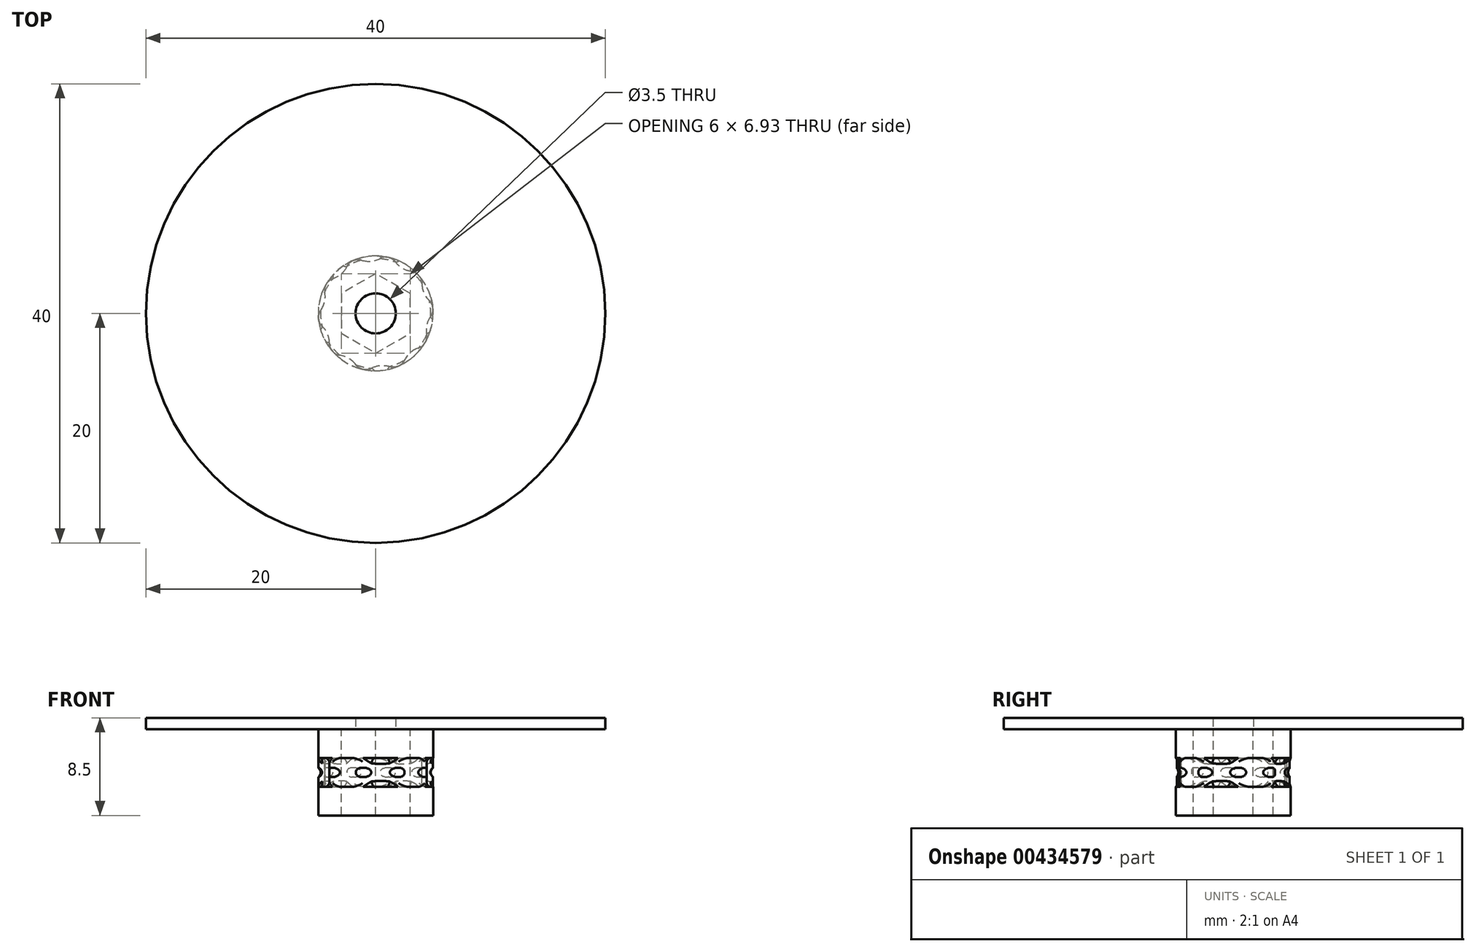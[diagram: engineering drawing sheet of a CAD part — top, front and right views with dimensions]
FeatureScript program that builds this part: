
annotation { "Feature Type Name" : "Feature", "Feature Type Description" : "" }
export const myFeature = defineFeature(function(context is Context, id is Id, definition is map)
    precondition{}
    {
        {
            var Q0;
            Q0=qCreatedBy(makeId("Top.planeOp"),FACE);
            var sketch = newSketch(context, id + "F0", { "sketchPlane" : qUnion([Q0])});
            skCircle(sketch, "E0", {"center": v(0, 0) * mm, "radius": 20 * mm});
            skCircle(sketch, "E1", {"center": v(0, 0) * mm, "radius": 1.75 * mm});
            skSolve(sketch);
        }
        {
            var Q0;
            Q0=makeQuery(id+"F0.imprint","IMPRINT",FACE,{"disambiguationData":[TD([[makeQuery(id+"F0.imprint","IMPRINT",EDGE,{"derivedFrom":sQuery(id+"F0.wireOp",EDGE,"E0")}),1.0]])]});
            extrude(context, id + "F1", {"entities" : qUnion([Q0]), "depth" : 1 * mm});
        }
        {
            var Q0;
            Q0=makeQuery(id+"F1.opExtrude","CAP_FACE",FACE,{"disambiguationData":[OSD([sQuery(id+"F0.wireOp",EDGE,"E0"),sQuery(id+"F0.wireOp",EDGE,"E1")])],"isStart":true});
            var sketch = newSketch(context, id + "F2", { "sketchPlane" : qUnion([Q0])});
            skCircle(sketch, "E2", {"center": v(0, 0) * mm, "radius": 5 * mm});
            skSolve(sketch);
        }
        {
            var Q0;
            Q0=makeQuery(id+"F2.imprint","IMPRINT",FACE,{"disambiguationData":[TD([[makeQuery(id+"F2.imprint","IMPRINT",EDGE,{"derivedFrom":sQuery(id+"F2.wireOp",EDGE,"E2")}),1.0]])]});
            var Q1;
            Q1=makeQuery(id+"F2.imprint","IMPRINT",FACE,{"disambiguationData":[TD([[makeQuery(id+"F2.imprint","IMPRINT",EDGE,{"derivedFrom":makeQuery(id+"F1.opExtrude","CAP_EDGE",EDGE,{"disambiguationData":[OSD([sQuery(id+"F0.wireOp",EDGE,"E1")])],"isStart":true})}),-1.0]])]});
            extrude(context, id + "F3", {"entities" : qUnion([Q0, Q1]), "depth" : 7.5 * mm, "offsetDistance" : 25 * mm});
        }
        {
            var Q0;
            Q0=makeQuery(id+"F3.opExtrude","CAP_FACE",FACE,{"disambiguationData":[OSD([sQuery(id+"F2.wireOp",EDGE,"E2")])],"isStart":true});
            var sketch = newSketch(context, id + "F4", { "sketchPlane" : qUnion([Q0])});
            skCircle(sketch, "E3.cCircle", {"center": v(0, 0) * mm, "radius": 3 * mm, "construction": true});
            skLineSegment(sketch, "E3.0", {"start": v(-3, -1.73) * mm, "end": v(-3, 1.73) * mm});
            skLineSegment(sketch, "E3.1", {"start": v(-3, 1.73) * mm, "end": v(0, 3.46) * mm});
            skLineSegment(sketch, "E3.2", {"start": v(0, 3.46) * mm, "end": v(3, 1.73) * mm});
            skLineSegment(sketch, "E3.3", {"start": v(3, 1.73) * mm, "end": v(3, -1.73) * mm});
            skLineSegment(sketch, "E3.4", {"start": v(3, -1.73) * mm, "end": v(0, -3.46) * mm});
            skLineSegment(sketch, "E3.5", {"start": v(0, -3.46) * mm, "end": v(-3, -1.73) * mm});
            skPoint(sketch, "E3.0.midPoint", {"position": v(-3, 0) * mm});
            skSolve(sketch);
        }
        {
            var Q0;
            Q0 = qSketchRegion(id + "F4", true);
            extrude(context, id + "F5", {"entities" : qUnion([Q0]), "operationType" : NewBodyOperationType.REMOVE, "endBound" : BoundingType.THROUGH_ALL, "oppositeDirection" : true, "depth" : 25 * mm});
        }
        {
            var Q0;
            Q0=makeQuery(id+"F3.opExtrude","CAP_FACE",FACE,{"disambiguationData":[OSD([sQuery(id+"F2.wireOp",EDGE,"E2")])],"isStart":false});
            cPlane(context, id + "F6", {"entities" : qUnion([Q0]), "cplaneType" : CPlaneType.OFFSET, "offset" : 3.75 * mm, "oppositeDirection" : true, "width" : 150 * mm, "height" : 150 * mm});
        }
        {
            var Q0;
            Q0=qCreatedBy(id+"F6.planeOp",FACE);
            var sketch = newSketch(context, id + "F7", { "sketchPlane" : qUnion([Q0])});
            skArc(sketch, "E4", {"start": v(-4.66, 1.12) * mm, "mid": v(-4.98, 0.5) * mm, "end": v(-4.8, -0.19) * mm});
            skArc(sketch, "E5", {"start": v(-4.66, 1.12) * mm, "mid": v(-4.2, 1.8) * mm, "end": v(-4.03, 2.6) * mm});
            skArc(sketch, "E6", {"start": v(-3.17, 3.6) * mm, "mid": v(-3.79, 3.27) * mm, "end": v(-4.03, 2.6) * mm});
            skPoint(sketch, "E7", {"position": v(-3.79, 3.27) * mm});
            skPoint(sketch, "E8", {"position": v(-4.2, 1.8) * mm});
            skPoint(sketch, "E9.positionSnap0", {"position": v(-4.98, 0.5) * mm});
            skCircle(sketch, "E10", {"center": v(0, 0) * mm, "radius": 5 * mm});
            skSolve(sketch);
        }
        {
            var Q0;
            {var subQ0=sQuery(id+"F7.wireOp",EDGE,"E5");Q0=makeQuery(id+"F7.imprint","IMPRINT",FACE,{"disambiguationData":[TD([[makeQuery(id+"F7.imprint","IMPRINT",EDGE,{"derivedFrom":subQ0}),1.0]])]});}
            extrude(context, id + "F8", {"entities" : qUnion([Q0]), "endBound" : BoundingType.SYMMETRIC, "depth" : 2.5 * mm});
        }
        {
            var Q0;
            Q0=qCreatedBy(makeId("Right.planeOp"),FACE);
            var sketch = newSketch(context, id + "F9", { "sketchPlane" : qUnion([Q0])});
            skLineSegment(sketch, "E11", {"start": v(0, 0) * mm, "end": v(0, -12.8) * mm});
            skSolve(sketch);
        }
        {
            var Q0;
            Q0=makeQuery(id+"F8.opExtrude","SWEPT_BODY",BODY,{"disambiguationData":[OSD([sQuery(id+"F7.wireOp",EDGE,"E4"),sQuery(id+"F7.wireOp",EDGE,"E5"),sQuery(id+"F7.wireOp",EDGE,"E6"),sQuery(id+"F7.wireOp",EDGE,"E10")])]});
            var Q1;
            Q1=sQuery(id+"F9.wireOp",EDGE,"E11");
            circularPattern(context, id + "F10", {"entities" : qUnion([Q0]), "axis" : qUnion([Q1]), "angle" : 360 * degree, "instanceCount" : 10, "equalSpace" : true});
        }
        {
            var Q0;
            Q0=makeQuery(id+"F10.opPattern","COPY",BODY,{"derivedFrom":makeQuery(id+"F8.opExtrude","SWEPT_BODY",BODY,{"disambiguationData":[OSD([sQuery(id+"F7.wireOp",EDGE,"E4"),sQuery(id+"F7.wireOp",EDGE,"E5"),sQuery(id+"F7.wireOp",EDGE,"E6"),sQuery(id+"F7.wireOp",EDGE,"E10")])]}),"instanceName":"6"});
            var Q1;
            Q1=makeQuery(id+"F10.opPattern","COPY",BODY,{"derivedFrom":makeQuery(id+"F8.opExtrude","SWEPT_BODY",BODY,{"disambiguationData":[OSD([sQuery(id+"F7.wireOp",EDGE,"E4"),sQuery(id+"F7.wireOp",EDGE,"E5"),sQuery(id+"F7.wireOp",EDGE,"E6"),sQuery(id+"F7.wireOp",EDGE,"E10")])]}),"instanceName":"5"});
            var Q2;
            Q2=makeQuery(id+"F10.opPattern","COPY",BODY,{"derivedFrom":makeQuery(id+"F8.opExtrude","SWEPT_BODY",BODY,{"disambiguationData":[OSD([sQuery(id+"F7.wireOp",EDGE,"E4"),sQuery(id+"F7.wireOp",EDGE,"E5"),sQuery(id+"F7.wireOp",EDGE,"E6"),sQuery(id+"F7.wireOp",EDGE,"E10")])]}),"instanceName":"7"});
            var Q3;
            Q3=makeQuery(id+"F10.opPattern","COPY",BODY,{"derivedFrom":makeQuery(id+"F8.opExtrude","SWEPT_BODY",BODY,{"disambiguationData":[OSD([sQuery(id+"F7.wireOp",EDGE,"E4"),sQuery(id+"F7.wireOp",EDGE,"E5"),sQuery(id+"F7.wireOp",EDGE,"E6"),sQuery(id+"F7.wireOp",EDGE,"E10")])]}),"instanceName":"24"});
            var Q4;
            Q4=makeQuery(id+"F10.opPattern","COPY",BODY,{"derivedFrom":makeQuery(id+"F8.opExtrude","SWEPT_BODY",BODY,{"disambiguationData":[OSD([sQuery(id+"F7.wireOp",EDGE,"E4"),sQuery(id+"F7.wireOp",EDGE,"E5"),sQuery(id+"F7.wireOp",EDGE,"E6"),sQuery(id+"F7.wireOp",EDGE,"E10")])]}),"instanceName":"23"});
            var Q5;
            Q5=makeQuery(id+"F10.opPattern","COPY",BODY,{"derivedFrom":makeQuery(id+"F8.opExtrude","SWEPT_BODY",BODY,{"disambiguationData":[OSD([sQuery(id+"F7.wireOp",EDGE,"E4"),sQuery(id+"F7.wireOp",EDGE,"E5"),sQuery(id+"F7.wireOp",EDGE,"E6"),sQuery(id+"F7.wireOp",EDGE,"E10")])]}),"instanceName":"22"});
            var Q6;
            Q6=makeQuery(id+"F10.opPattern","COPY",BODY,{"derivedFrom":makeQuery(id+"F8.opExtrude","SWEPT_BODY",BODY,{"disambiguationData":[OSD([sQuery(id+"F7.wireOp",EDGE,"E4"),sQuery(id+"F7.wireOp",EDGE,"E5"),sQuery(id+"F7.wireOp",EDGE,"E6"),sQuery(id+"F7.wireOp",EDGE,"E10")])]}),"instanceName":"21"});
            var Q7;
            Q7=makeQuery(id+"F10.opPattern","COPY",BODY,{"derivedFrom":makeQuery(id+"F8.opExtrude","SWEPT_BODY",BODY,{"disambiguationData":[OSD([sQuery(id+"F7.wireOp",EDGE,"E4"),sQuery(id+"F7.wireOp",EDGE,"E5"),sQuery(id+"F7.wireOp",EDGE,"E6"),sQuery(id+"F7.wireOp",EDGE,"E10")])]}),"instanceName":"20"});
            var Q8;
            Q8=makeQuery(id+"F10.opPattern","COPY",BODY,{"derivedFrom":makeQuery(id+"F8.opExtrude","SWEPT_BODY",BODY,{"disambiguationData":[OSD([sQuery(id+"F7.wireOp",EDGE,"E4"),sQuery(id+"F7.wireOp",EDGE,"E5"),sQuery(id+"F7.wireOp",EDGE,"E6"),sQuery(id+"F7.wireOp",EDGE,"E10")])]}),"instanceName":"19"});
            var Q9;
            Q9=makeQuery(id+"F10.opPattern","COPY",BODY,{"derivedFrom":makeQuery(id+"F8.opExtrude","SWEPT_BODY",BODY,{"disambiguationData":[OSD([sQuery(id+"F7.wireOp",EDGE,"E4"),sQuery(id+"F7.wireOp",EDGE,"E5"),sQuery(id+"F7.wireOp",EDGE,"E6"),sQuery(id+"F7.wireOp",EDGE,"E10")])]}),"instanceName":"18"});
            var Q10;
            Q10=makeQuery(id+"F10.opPattern","COPY",BODY,{"derivedFrom":makeQuery(id+"F8.opExtrude","SWEPT_BODY",BODY,{"disambiguationData":[OSD([sQuery(id+"F7.wireOp",EDGE,"E4"),sQuery(id+"F7.wireOp",EDGE,"E5"),sQuery(id+"F7.wireOp",EDGE,"E6"),sQuery(id+"F7.wireOp",EDGE,"E10")])]}),"instanceName":"17"});
            var Q11;
            Q11=makeQuery(id+"F10.opPattern","COPY",BODY,{"derivedFrom":makeQuery(id+"F8.opExtrude","SWEPT_BODY",BODY,{"disambiguationData":[OSD([sQuery(id+"F7.wireOp",EDGE,"E4"),sQuery(id+"F7.wireOp",EDGE,"E5"),sQuery(id+"F7.wireOp",EDGE,"E6"),sQuery(id+"F7.wireOp",EDGE,"E10")])]}),"instanceName":"16"});
            var Q12;
            Q12=makeQuery(id+"F10.opPattern","COPY",BODY,{"derivedFrom":makeQuery(id+"F8.opExtrude","SWEPT_BODY",BODY,{"disambiguationData":[OSD([sQuery(id+"F7.wireOp",EDGE,"E4"),sQuery(id+"F7.wireOp",EDGE,"E5"),sQuery(id+"F7.wireOp",EDGE,"E6"),sQuery(id+"F7.wireOp",EDGE,"E10")])]}),"instanceName":"15"});
            var Q13;
            Q13=makeQuery(id+"F10.opPattern","COPY",BODY,{"derivedFrom":makeQuery(id+"F8.opExtrude","SWEPT_BODY",BODY,{"disambiguationData":[OSD([sQuery(id+"F7.wireOp",EDGE,"E4"),sQuery(id+"F7.wireOp",EDGE,"E5"),sQuery(id+"F7.wireOp",EDGE,"E6"),sQuery(id+"F7.wireOp",EDGE,"E10")])]}),"instanceName":"14"});
            var Q14;
            Q14=makeQuery(id+"F10.opPattern","COPY",BODY,{"derivedFrom":makeQuery(id+"F8.opExtrude","SWEPT_BODY",BODY,{"disambiguationData":[OSD([sQuery(id+"F7.wireOp",EDGE,"E4"),sQuery(id+"F7.wireOp",EDGE,"E5"),sQuery(id+"F7.wireOp",EDGE,"E6"),sQuery(id+"F7.wireOp",EDGE,"E10")])]}),"instanceName":"13"});
            var Q15;
            Q15=makeQuery(id+"F10.opPattern","COPY",BODY,{"derivedFrom":makeQuery(id+"F8.opExtrude","SWEPT_BODY",BODY,{"disambiguationData":[OSD([sQuery(id+"F7.wireOp",EDGE,"E4"),sQuery(id+"F7.wireOp",EDGE,"E5"),sQuery(id+"F7.wireOp",EDGE,"E6"),sQuery(id+"F7.wireOp",EDGE,"E10")])]}),"instanceName":"10"});
            var Q16;
            Q16=makeQuery(id+"F10.opPattern","COPY",BODY,{"derivedFrom":makeQuery(id+"F8.opExtrude","SWEPT_BODY",BODY,{"disambiguationData":[OSD([sQuery(id+"F7.wireOp",EDGE,"E4"),sQuery(id+"F7.wireOp",EDGE,"E5"),sQuery(id+"F7.wireOp",EDGE,"E6"),sQuery(id+"F7.wireOp",EDGE,"E10")])]}),"instanceName":"1"});
            var Q17;
            Q17=makeQuery(id+"F10.opPattern","COPY",BODY,{"derivedFrom":makeQuery(id+"F8.opExtrude","SWEPT_BODY",BODY,{"disambiguationData":[OSD([sQuery(id+"F7.wireOp",EDGE,"E4"),sQuery(id+"F7.wireOp",EDGE,"E5"),sQuery(id+"F7.wireOp",EDGE,"E6"),sQuery(id+"F7.wireOp",EDGE,"E10")])]}),"instanceName":"11"});
            var Q18;
            Q18=makeQuery(id+"F10.opPattern","COPY",BODY,{"derivedFrom":makeQuery(id+"F8.opExtrude","SWEPT_BODY",BODY,{"disambiguationData":[OSD([sQuery(id+"F7.wireOp",EDGE,"E4"),sQuery(id+"F7.wireOp",EDGE,"E5"),sQuery(id+"F7.wireOp",EDGE,"E6"),sQuery(id+"F7.wireOp",EDGE,"E10")])]}),"instanceName":"2"});
            var Q19;
            Q19=makeQuery(id+"F10.opPattern","COPY",BODY,{"derivedFrom":makeQuery(id+"F8.opExtrude","SWEPT_BODY",BODY,{"disambiguationData":[OSD([sQuery(id+"F7.wireOp",EDGE,"E4"),sQuery(id+"F7.wireOp",EDGE,"E5"),sQuery(id+"F7.wireOp",EDGE,"E6"),sQuery(id+"F7.wireOp",EDGE,"E10")])]}),"instanceName":"9"});
            var Q20;
            Q20=makeQuery(id+"F8.opExtrude","SWEPT_BODY",BODY,{"disambiguationData":[OSD([sQuery(id+"F7.wireOp",EDGE,"E4"),sQuery(id+"F7.wireOp",EDGE,"E5"),sQuery(id+"F7.wireOp",EDGE,"E6"),sQuery(id+"F7.wireOp",EDGE,"E10")])]});
            var Q21;
            Q21=makeQuery(id+"F10.opPattern","COPY",BODY,{"derivedFrom":makeQuery(id+"F8.opExtrude","SWEPT_BODY",BODY,{"disambiguationData":[OSD([sQuery(id+"F7.wireOp",EDGE,"E4"),sQuery(id+"F7.wireOp",EDGE,"E5"),sQuery(id+"F7.wireOp",EDGE,"E6"),sQuery(id+"F7.wireOp",EDGE,"E10")])]}),"instanceName":"8"});
            var Q22;
            Q22=makeQuery(id+"F10.opPattern","COPY",BODY,{"derivedFrom":makeQuery(id+"F8.opExtrude","SWEPT_BODY",BODY,{"disambiguationData":[OSD([sQuery(id+"F7.wireOp",EDGE,"E4"),sQuery(id+"F7.wireOp",EDGE,"E5"),sQuery(id+"F7.wireOp",EDGE,"E6"),sQuery(id+"F7.wireOp",EDGE,"E10")])]}),"instanceName":"4"});
            var Q23;
            Q23=makeQuery(id+"F10.opPattern","COPY",BODY,{"derivedFrom":makeQuery(id+"F8.opExtrude","SWEPT_BODY",BODY,{"disambiguationData":[OSD([sQuery(id+"F7.wireOp",EDGE,"E4"),sQuery(id+"F7.wireOp",EDGE,"E5"),sQuery(id+"F7.wireOp",EDGE,"E6"),sQuery(id+"F7.wireOp",EDGE,"E10")])]}),"instanceName":"12"});
            var Q24;
            Q24=makeQuery(id+"F10.opPattern","COPY",BODY,{"derivedFrom":makeQuery(id+"F8.opExtrude","SWEPT_BODY",BODY,{"disambiguationData":[OSD([sQuery(id+"F7.wireOp",EDGE,"E4"),sQuery(id+"F7.wireOp",EDGE,"E5"),sQuery(id+"F7.wireOp",EDGE,"E6"),sQuery(id+"F7.wireOp",EDGE,"E10")])]}),"instanceName":"3"});
            var Q25;
            Q25=makeQuery(id+"F3.opExtrude","SWEPT_BODY",BODY,{"disambiguationData":[OSD([sQuery(id+"F2.wireOp",EDGE,"E2")])]});
            booleanBodies(context, id + "F11", {"operationType" : BooleanOperationType.SUBTRACTION, "tools" : qUnion([Q0, Q1, Q2, Q3, Q4, Q5, Q6, Q7, Q8, Q9, Q10, Q11, Q12, Q13, Q14, Q15, Q16, Q17, Q18, Q19, Q20, Q21, Q22, Q23, Q24]), "targets" : qUnion([Q25])});
        }
        {
            var Q0;
            Q0=qCreatedBy(makeId("Right.planeOp"),FACE);
            var sketch = newSketch(context, id + "F12", { "sketchPlane" : qUnion([Q0])});
            skPoint(sketch, "E12", {"position": v(-5, -2.5) * mm});
            skPoint(sketch, "E13", {"position": v(-5, -5) * mm});
            skArc(sketch, "E14", {"start": v(-5, -4.15) * mm, "mid": v(-4.8, -3.75) * mm, "end": v(-5, -3.35) * mm});
            skLineSegment(sketch, "E15", {"start": v(-5, -2.5) * mm, "end": v(-5, -5) * mm, "construction": true});
            skPoint(sketch, "E16", {"position": v(-5, -3.75) * mm});
            skPoint(sketch, "E17", {"position": v(-4.8, -3.75) * mm});
            skLineSegment(sketch, "E18", {"start": v(-5, -3.35) * mm, "end": v(-5, -4.15) * mm});
            skSolve(sketch);
        }
        {
            var Q0;
            Q0=qCreatedBy(makeId("Right.planeOp"),FACE);
            var sketch = newSketch(context, id + "F13", { "sketchPlane" : qUnion([Q0])});
            skLineSegment(sketch, "E19", {"start": v(0, 0) * mm, "end": v(0, 14) * mm});
            skSolve(sketch);
        }
        {
            var Q0;
            Q0=makeQuery(id+"F11.opBoolean","COPY",EDGE,{"derivedFrom":makeQuery(id+"F10.opPattern","COPY",EDGE,{"derivedFrom":makeQuery(id+"F8.opExtrude","CAP_EDGE",EDGE,{"disambiguationData":[OSD([sQuery(id+"F7.wireOp",EDGE,"E5")])],"isStart":true}),"instanceName":"15"})});
            var Q1;
            Q1=makeQuery(id+"F11.opBoolean","COPY",EDGE,{"derivedFrom":makeQuery(id+"F10.opPattern","COPY",EDGE,{"derivedFrom":makeQuery(id+"F8.opExtrude","CAP_EDGE",EDGE,{"disambiguationData":[OSD([sQuery(id+"F7.wireOp",EDGE,"E5")])],"isStart":true}),"instanceName":"13"})});
            var Q2;
            Q2=makeQuery(id+"F11.opBoolean","COPY",EDGE,{"derivedFrom":makeQuery(id+"F10.opPattern","COPY",EDGE,{"derivedFrom":makeQuery(id+"F8.opExtrude","CAP_EDGE",EDGE,{"disambiguationData":[OSD([sQuery(id+"F7.wireOp",EDGE,"E5")])],"isStart":true}),"instanceName":"11"})});
            var Q3;
            Q3=makeQuery(id+"F11.opBoolean","COPY",EDGE,{"derivedFrom":makeQuery(id+"F10.opPattern","COPY",EDGE,{"derivedFrom":makeQuery(id+"F8.opExtrude","CAP_EDGE",EDGE,{"disambiguationData":[OSD([sQuery(id+"F7.wireOp",EDGE,"E5")])],"isStart":true}),"instanceName":"9"})});
            var Q4;
            Q4=makeQuery(id+"F11.opBoolean","COPY",EDGE,{"derivedFrom":makeQuery(id+"F10.opPattern","COPY",EDGE,{"derivedFrom":makeQuery(id+"F8.opExtrude","CAP_EDGE",EDGE,{"disambiguationData":[OSD([sQuery(id+"F7.wireOp",EDGE,"E5")])],"isStart":true}),"instanceName":"17"})});
            var Q5;
            Q5=makeQuery(id+"F11.opBoolean","COPY",EDGE,{"derivedFrom":makeQuery(id+"F10.opPattern","COPY",EDGE,{"derivedFrom":makeQuery(id+"F8.opExtrude","CAP_EDGE",EDGE,{"disambiguationData":[OSD([sQuery(id+"F7.wireOp",EDGE,"E5")])],"isStart":true}),"instanceName":"1"})});
            var Q6;
            Q6=makeQuery(id+"F11.opBoolean","COPY",EDGE,{"derivedFrom":makeQuery(id+"F10.opPattern","COPY",EDGE,{"derivedFrom":makeQuery(id+"F8.opExtrude","CAP_EDGE",EDGE,{"disambiguationData":[OSD([sQuery(id+"F7.wireOp",EDGE,"E5")])],"isStart":true}),"instanceName":"3"})});
            var Q7;
            Q7=makeQuery(id+"F11.opBoolean","COPY",EDGE,{"derivedFrom":makeQuery(id+"F10.opPattern","COPY",EDGE,{"derivedFrom":makeQuery(id+"F8.opExtrude","CAP_EDGE",EDGE,{"disambiguationData":[OSD([sQuery(id+"F7.wireOp",EDGE,"E5")])],"isStart":true}),"instanceName":"5"})});
            var Q8;
            Q8=makeQuery(id+"F11.opBoolean","COPY",EDGE,{"derivedFrom":makeQuery(id+"F10.opPattern","COPY",EDGE,{"derivedFrom":makeQuery(id+"F8.opExtrude","CAP_EDGE",EDGE,{"disambiguationData":[OSD([sQuery(id+"F7.wireOp",EDGE,"E5")])],"isStart":true}),"instanceName":"7"})});
            var Q9;
            Q9=makeQuery(id+"F11.opBoolean","COPY",EDGE,{"derivedFrom":makeQuery(id+"F10.opPattern","COPY",EDGE,{"derivedFrom":makeQuery(id+"F8.opExtrude","CAP_EDGE",EDGE,{"disambiguationData":[OSD([sQuery(id+"F7.wireOp",EDGE,"E5")])],"isStart":false}),"instanceName":"7"})});
            var Q10;
            Q10=makeQuery(id+"F11.opBoolean","COPY",EDGE,{"derivedFrom":makeQuery(id+"F10.opPattern","COPY",EDGE,{"derivedFrom":makeQuery(id+"F8.opExtrude","CAP_EDGE",EDGE,{"disambiguationData":[OSD([sQuery(id+"F7.wireOp",EDGE,"E5")])],"isStart":false}),"instanceName":"5"})});
            var Q11;
            Q11=makeQuery(id+"F11.opBoolean","COPY",EDGE,{"derivedFrom":makeQuery(id+"F10.opPattern","COPY",EDGE,{"derivedFrom":makeQuery(id+"F8.opExtrude","CAP_EDGE",EDGE,{"disambiguationData":[OSD([sQuery(id+"F7.wireOp",EDGE,"E5")])],"isStart":false}),"instanceName":"3"})});
            var Q12;
            Q12=makeQuery(id+"F11.opBoolean","COPY",EDGE,{"derivedFrom":makeQuery(id+"F10.opPattern","COPY",EDGE,{"derivedFrom":makeQuery(id+"F8.opExtrude","CAP_EDGE",EDGE,{"disambiguationData":[OSD([sQuery(id+"F7.wireOp",EDGE,"E5")])],"isStart":false}),"instanceName":"1"})});
            var Q13;
            Q13=makeQuery(id+"F11.opBoolean","COPY",EDGE,{"derivedFrom":makeQuery(id+"F10.opPattern","COPY",EDGE,{"derivedFrom":makeQuery(id+"F8.opExtrude","CAP_EDGE",EDGE,{"disambiguationData":[OSD([sQuery(id+"F7.wireOp",EDGE,"E5")])],"isStart":false}),"instanceName":"17"})});
            var Q14;
            Q14=makeQuery(id+"F11.opBoolean","COPY",EDGE,{"derivedFrom":makeQuery(id+"F10.opPattern","COPY",EDGE,{"derivedFrom":makeQuery(id+"F8.opExtrude","CAP_EDGE",EDGE,{"disambiguationData":[OSD([sQuery(id+"F7.wireOp",EDGE,"E5")])],"isStart":false}),"instanceName":"15"})});
            var Q15;
            Q15=makeQuery(id+"F11.opBoolean","COPY",EDGE,{"derivedFrom":makeQuery(id+"F10.opPattern","COPY",EDGE,{"derivedFrom":makeQuery(id+"F8.opExtrude","CAP_EDGE",EDGE,{"disambiguationData":[OSD([sQuery(id+"F7.wireOp",EDGE,"E5")])],"isStart":false}),"instanceName":"13"})});
            var Q16;
            Q16=makeQuery(id+"F11.opBoolean","COPY",EDGE,{"derivedFrom":makeQuery(id+"F10.opPattern","COPY",EDGE,{"derivedFrom":makeQuery(id+"F8.opExtrude","CAP_EDGE",EDGE,{"disambiguationData":[OSD([sQuery(id+"F7.wireOp",EDGE,"E5")])],"isStart":false}),"instanceName":"11"})});
            var Q17;
            Q17=makeQuery(id+"F11.opBoolean","COPY",EDGE,{"derivedFrom":makeQuery(id+"F10.opPattern","COPY",EDGE,{"derivedFrom":makeQuery(id+"F8.opExtrude","CAP_EDGE",EDGE,{"disambiguationData":[OSD([sQuery(id+"F7.wireOp",EDGE,"E5")])],"isStart":false}),"instanceName":"9"})});
            fillet(context, id + "F14", {"entities" : qUnion([Q0, Q1, Q2, Q3, Q4, Q5, Q6, Q7, Q8, Q9, Q10, Q11, Q12, Q13, Q14, Q15, Q16, Q17]), "radius" : 0.3 * mm, "tangentPropagation" : true, "allowEdgeOverflow" : false});
        }
        {
            var Q0;
            Q0=makeQuery(id+"F11.opBoolean","COPY",EDGE,{"derivedFrom":makeQuery(id+"F10.opPattern","COPY",EDGE,{"derivedFrom":makeQuery(id+"F8.opExtrude","CAP_EDGE",EDGE,{"disambiguationData":[OSD([sQuery(id+"F7.wireOp",EDGE,"E5")])],"isStart":false}),"instanceName":"8"})});
            var Q1;
            Q1=makeQuery(id+"F11.opBoolean","COPY",EDGE,{"derivedFrom":makeQuery(id+"F10.opPattern","COPY",EDGE,{"derivedFrom":makeQuery(id+"F8.opExtrude","CAP_EDGE",EDGE,{"disambiguationData":[OSD([sQuery(id+"F7.wireOp",EDGE,"E5")])],"isStart":true}),"instanceName":"8"})});
            var Q2;
            Q2=makeQuery(id+"F11.opBoolean","COPY",EDGE,{"derivedFrom":makeQuery(id+"F10.opPattern","COPY",EDGE,{"derivedFrom":makeQuery(id+"F8.opExtrude","CAP_EDGE",EDGE,{"disambiguationData":[OSD([sQuery(id+"F7.wireOp",EDGE,"E5")])],"isStart":true}),"instanceName":"6"})});
            var Q3;
            Q3=makeQuery(id+"F11.opBoolean","COPY",EDGE,{"derivedFrom":makeQuery(id+"F10.opPattern","COPY",EDGE,{"derivedFrom":makeQuery(id+"F8.opExtrude","CAP_EDGE",EDGE,{"disambiguationData":[OSD([sQuery(id+"F7.wireOp",EDGE,"E5")])],"isStart":false}),"instanceName":"6"})});
            var Q4;
            Q4=makeQuery(id+"F11.opBoolean","COPY",EDGE,{"derivedFrom":makeQuery(id+"F10.opPattern","COPY",EDGE,{"derivedFrom":makeQuery(id+"F8.opExtrude","CAP_EDGE",EDGE,{"disambiguationData":[OSD([sQuery(id+"F7.wireOp",EDGE,"E5")])],"isStart":false}),"instanceName":"4"})});
            var Q5;
            Q5=makeQuery(id+"F11.opBoolean","COPY",EDGE,{"derivedFrom":makeQuery(id+"F10.opPattern","COPY",EDGE,{"derivedFrom":makeQuery(id+"F8.opExtrude","CAP_EDGE",EDGE,{"disambiguationData":[OSD([sQuery(id+"F7.wireOp",EDGE,"E5")])],"isStart":true}),"instanceName":"4"})});
            var Q6;
            Q6=makeQuery(id+"F11.opBoolean","COPY",EDGE,{"derivedFrom":makeQuery(id+"F10.opPattern","COPY",EDGE,{"derivedFrom":makeQuery(id+"F8.opExtrude","CAP_EDGE",EDGE,{"disambiguationData":[OSD([sQuery(id+"F7.wireOp",EDGE,"E5")])],"isStart":false}),"instanceName":"2"})});
            var Q7;
            Q7=makeQuery(id+"F11.opBoolean","COPY",EDGE,{"derivedFrom":makeQuery(id+"F10.opPattern","COPY",EDGE,{"derivedFrom":makeQuery(id+"F8.opExtrude","CAP_EDGE",EDGE,{"disambiguationData":[OSD([sQuery(id+"F7.wireOp",EDGE,"E5")])],"isStart":true}),"instanceName":"2"})});
            var Q8;
            Q8=makeQuery(id+"F11.opBoolean","COPY",EDGE,{"derivedFrom":makeQuery(id+"F8.opExtrude","CAP_EDGE",EDGE,{"disambiguationData":[OSD([sQuery(id+"F7.wireOp",EDGE,"E5")])],"isStart":true})});
            var Q9;
            Q9=makeQuery(id+"F11.opBoolean","COPY",EDGE,{"derivedFrom":makeQuery(id+"F8.opExtrude","CAP_EDGE",EDGE,{"disambiguationData":[OSD([sQuery(id+"F7.wireOp",EDGE,"E5")])],"isStart":false})});
            var Q10;
            Q10=makeQuery(id+"F11.opBoolean","COPY",EDGE,{"derivedFrom":makeQuery(id+"F10.opPattern","COPY",EDGE,{"derivedFrom":makeQuery(id+"F8.opExtrude","CAP_EDGE",EDGE,{"disambiguationData":[OSD([sQuery(id+"F7.wireOp",EDGE,"E5")])],"isStart":false}),"instanceName":"16"})});
            var Q11;
            Q11=makeQuery(id+"F11.opBoolean","COPY",EDGE,{"derivedFrom":makeQuery(id+"F10.opPattern","COPY",EDGE,{"derivedFrom":makeQuery(id+"F8.opExtrude","CAP_EDGE",EDGE,{"disambiguationData":[OSD([sQuery(id+"F7.wireOp",EDGE,"E5")])],"isStart":true}),"instanceName":"16"})});
            var Q12;
            Q12=makeQuery(id+"F11.opBoolean","COPY",EDGE,{"derivedFrom":makeQuery(id+"F10.opPattern","COPY",EDGE,{"derivedFrom":makeQuery(id+"F8.opExtrude","CAP_EDGE",EDGE,{"disambiguationData":[OSD([sQuery(id+"F7.wireOp",EDGE,"E5")])],"isStart":false}),"instanceName":"14"})});
            var Q13;
            Q13=makeQuery(id+"F11.opBoolean","COPY",EDGE,{"derivedFrom":makeQuery(id+"F10.opPattern","COPY",EDGE,{"derivedFrom":makeQuery(id+"F8.opExtrude","CAP_EDGE",EDGE,{"disambiguationData":[OSD([sQuery(id+"F7.wireOp",EDGE,"E5")])],"isStart":true}),"instanceName":"14"})});
            var Q14;
            Q14=makeQuery(id+"F11.opBoolean","COPY",EDGE,{"derivedFrom":makeQuery(id+"F10.opPattern","COPY",EDGE,{"derivedFrom":makeQuery(id+"F8.opExtrude","CAP_EDGE",EDGE,{"disambiguationData":[OSD([sQuery(id+"F7.wireOp",EDGE,"E5")])],"isStart":true}),"instanceName":"12"})});
            var Q15;
            Q15=makeQuery(id+"F11.opBoolean","COPY",EDGE,{"derivedFrom":makeQuery(id+"F10.opPattern","COPY",EDGE,{"derivedFrom":makeQuery(id+"F8.opExtrude","CAP_EDGE",EDGE,{"disambiguationData":[OSD([sQuery(id+"F7.wireOp",EDGE,"E5")])],"isStart":false}),"instanceName":"12"})});
            var Q16;
            Q16=makeQuery(id+"F11.opBoolean","COPY",EDGE,{"derivedFrom":makeQuery(id+"F10.opPattern","COPY",EDGE,{"derivedFrom":makeQuery(id+"F8.opExtrude","CAP_EDGE",EDGE,{"disambiguationData":[OSD([sQuery(id+"F7.wireOp",EDGE,"E5")])],"isStart":true}),"instanceName":"10"})});
            var Q17;
            Q17=makeQuery(id+"F11.opBoolean","COPY",EDGE,{"derivedFrom":makeQuery(id+"F10.opPattern","COPY",EDGE,{"derivedFrom":makeQuery(id+"F8.opExtrude","CAP_EDGE",EDGE,{"disambiguationData":[OSD([sQuery(id+"F7.wireOp",EDGE,"E5")])],"isStart":false}),"instanceName":"10"})});
            fillet(context, id + "F15", {"entities" : qUnion([Q0, Q1, Q2, Q3, Q4, Q5, Q6, Q7, Q8, Q9, Q10, Q11, Q12, Q13, Q14, Q15, Q16, Q17]), "radius" : 0.5 * mm, "tangentPropagation" : true, "allowEdgeOverflow" : false});
        }
        {
            var Q0;
            Q0=makeQuery(id+"F12.imprint","IMPRINT",FACE,{"disambiguationData":[TD([[makeQuery(id+"F12.imprint","IMPRINT",EDGE,{"derivedFrom":sQuery(id+"F12.wireOp",EDGE,"E14")}),1.0]])]});
            var Q1;
            Q1=sQuery(id+"F13.wireOp",EDGE,"E19");
            revolve(context, id + "F16", {"operationType" : NewBodyOperationType.REMOVE, "entities" : qUnion([Q0]), "axis" : qUnion([Q1]), "revolveType" : RevolveType.FULL, "oppositeDirection" : true});
        }
    });
